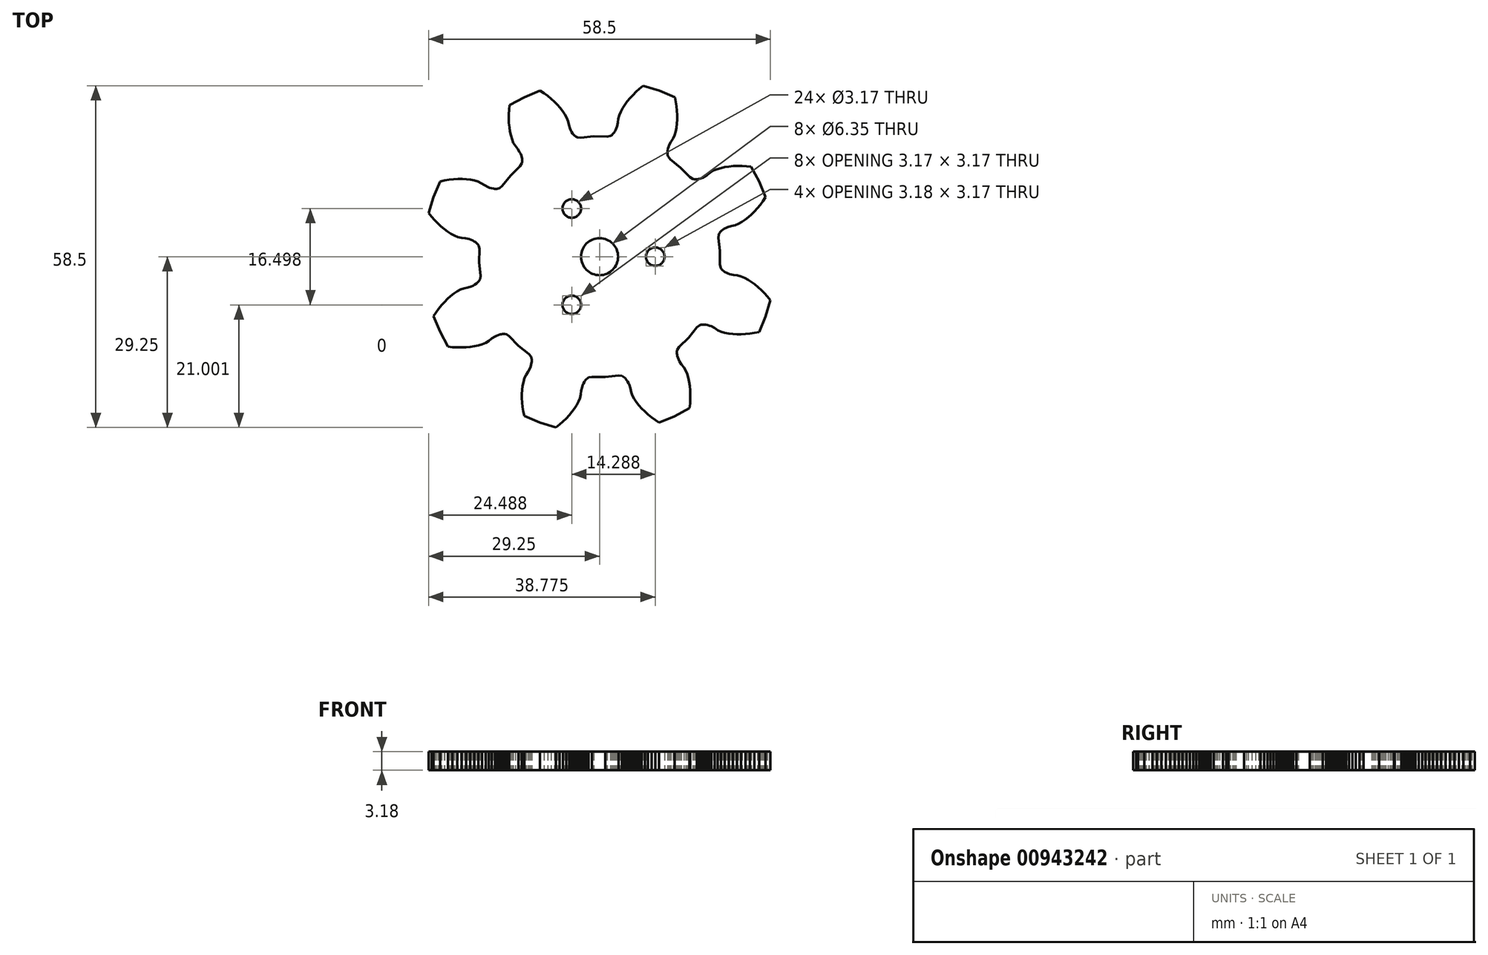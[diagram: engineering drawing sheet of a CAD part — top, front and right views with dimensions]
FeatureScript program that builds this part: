
annotation { "Feature Type Name" : "Feature", "Feature Type Description" : "" }
export const myFeature = defineFeature(function(context is Context, id is Id, definition is map)
    precondition{}
    {
        {
            var Q0;
            Q0=qCreatedBy(makeId("Top.planeOp"),FACE);
            var sketch = newSketch(context, id + "F0", { "sketchPlane" : qUnion([Q0])});
            skLineSegment(sketch, "E0", {"start": v(-20.57, 1.3) * mm, "end": v(-20.69, 1.86) * mm});
            skLineSegment(sketch, "E1", {"start": v(-20.69, 1.86) * mm, "end": v(-20.83, 2.1) * mm});
            skLineSegment(sketch, "E2", {"start": v(-20.83, 2.1) * mm, "end": v(-20.97, 2.26) * mm});
            skLineSegment(sketch, "E3", {"start": v(-20.97, 2.26) * mm, "end": v(-21.12, 2.4) * mm});
            skLineSegment(sketch, "E4", {"start": v(-21.12, 2.4) * mm, "end": v(-21.26, 2.5) * mm});
            skLineSegment(sketch, "E5", {"start": v(-21.26, 2.5) * mm, "end": v(-21.41, 2.6) * mm});
            skLineSegment(sketch, "E6", {"start": v(-21.41, 2.6) * mm, "end": v(-21.71, 2.77) * mm});
            skLineSegment(sketch, "E7", {"start": v(-21.71, 2.77) * mm, "end": v(-22.02, 2.9) * mm});
            skLineSegment(sketch, "E8", {"start": v(-22.02, 2.9) * mm, "end": v(-22.33, 3) * mm});
            skLineSegment(sketch, "E9", {"start": v(-22.33, 3) * mm, "end": v(-22.95, 3.13) * mm});
            skLineSegment(sketch, "E10", {"start": v(-22.95, 3.13) * mm, "end": v(-23.59, 3.2) * mm});
            skLineSegment(sketch, "E11", {"start": v(-23.59, 3.2) * mm, "end": v(-24.21, 3.36) * mm});
            skLineSegment(sketch, "E12", {"start": v(-24.21, 3.36) * mm, "end": v(-24.82, 3.62) * mm});
            skLineSegment(sketch, "E13", {"start": v(-24.82, 3.62) * mm, "end": v(-25.41, 3.95) * mm});
            skLineSegment(sketch, "E14", {"start": v(-25.41, 3.95) * mm, "end": v(-26, 4.32) * mm});
            skLineSegment(sketch, "E15", {"start": v(-26, 4.32) * mm, "end": v(-26.58, 4.74) * mm});
            skLineSegment(sketch, "E16", {"start": v(-26.58, 4.74) * mm, "end": v(-27.14, 5.2) * mm});
            skLineSegment(sketch, "E17", {"start": v(-27.14, 5.2) * mm, "end": v(-27.69, 5.71) * mm});
            skLineSegment(sketch, "E18", {"start": v(-27.69, 5.71) * mm, "end": v(-28.22, 6.26) * mm});
            skLineSegment(sketch, "E19", {"start": v(-28.22, 6.26) * mm, "end": v(-28.74, 6.84) * mm});
            skLineSegment(sketch, "E20", {"start": v(-28.74, 6.84) * mm, "end": v(-29.25, 7.46) * mm});
            skLineSegment(sketch, "E21", {"start": v(-29.25, 7.46) * mm, "end": v(-28.4, 10.23) * mm});
            skLineSegment(sketch, "E22", {"start": v(-28.4, 10.23) * mm, "end": v(-27.3, 12.9) * mm});
            skLineSegment(sketch, "E23", {"start": v(-27.3, 12.9) * mm, "end": v(-26.5, 13.05) * mm});
            skLineSegment(sketch, "E24", {"start": v(-26.5, 13.05) * mm, "end": v(-25.74, 13.17) * mm});
            skLineSegment(sketch, "E25", {"start": v(-25.74, 13.17) * mm, "end": v(-24.98, 13.25) * mm});
            skLineSegment(sketch, "E26", {"start": v(-24.98, 13.25) * mm, "end": v(-24.23, 13.29) * mm});
            skLineSegment(sketch, "E27", {"start": v(-24.23, 13.29) * mm, "end": v(-23.5, 13.29) * mm});
            skLineSegment(sketch, "E28", {"start": v(-23.5, 13.29) * mm, "end": v(-22.79, 13.24) * mm});
            skLineSegment(sketch, "E29", {"start": v(-22.79, 13.24) * mm, "end": v(-22.1, 13.16) * mm});
            skLineSegment(sketch, "E30", {"start": v(-22.1, 13.16) * mm, "end": v(-21.43, 13.03) * mm});
            skLineSegment(sketch, "E31", {"start": v(-21.43, 13.03) * mm, "end": v(-20.8, 12.85) * mm});
            skLineSegment(sketch, "E32", {"start": v(-20.8, 12.85) * mm, "end": v(-20.21, 12.57) * mm});
            skLineSegment(sketch, "E33", {"start": v(-20.21, 12.57) * mm, "end": v(-19.68, 12.22) * mm});
            skLineSegment(sketch, "E34", {"start": v(-19.68, 12.22) * mm, "end": v(-19.11, 11.92) * mm});
            skLineSegment(sketch, "E35", {"start": v(-19.11, 11.92) * mm, "end": v(-18.81, 11.8) * mm});
            skLineSegment(sketch, "E36", {"start": v(-18.81, 11.8) * mm, "end": v(-18.5, 11.7) * mm});
            skLineSegment(sketch, "E37", {"start": v(-18.5, 11.7) * mm, "end": v(-18.16, 11.64) * mm});
            skLineSegment(sketch, "E38", {"start": v(-18.16, 11.64) * mm, "end": v(-17.98, 11.62) * mm});
            skLineSegment(sketch, "E39", {"start": v(-17.98, 11.62) * mm, "end": v(-17.8, 11.62) * mm});
            skLineSegment(sketch, "E40", {"start": v(-17.8, 11.62) * mm, "end": v(-17.6, 11.63) * mm});
            skLineSegment(sketch, "E41", {"start": v(-17.6, 11.63) * mm, "end": v(-17.38, 11.67) * mm});
            skLineSegment(sketch, "E42", {"start": v(-17.38, 11.67) * mm, "end": v(-17.13, 11.75) * mm});
            skLineSegment(sketch, "E43", {"start": v(-17.13, 11.75) * mm, "end": v(-16.68, 12.1) * mm});
            skLineSegment(sketch, "E44", {"start": v(-16.68, 12.1) * mm, "end": v(-15.25, 13.87) * mm});
            skLineSegment(sketch, "E45", {"start": v(-15.25, 13.87) * mm, "end": v(-13.62, 15.47) * mm});
            skLineSegment(sketch, "E46", {"start": v(-13.62, 15.47) * mm, "end": v(-13.31, 15.95) * mm});
            skLineSegment(sketch, "E47", {"start": v(-13.31, 15.95) * mm, "end": v(-13.25, 16.2) * mm});
            skLineSegment(sketch, "E48", {"start": v(-13.25, 16.2) * mm, "end": v(-13.23, 16.43) * mm});
            skLineSegment(sketch, "E49", {"start": v(-13.23, 16.43) * mm, "end": v(-13.24, 16.62) * mm});
            skLineSegment(sketch, "E50", {"start": v(-13.24, 16.62) * mm, "end": v(-13.26, 16.8) * mm});
            skLineSegment(sketch, "E51", {"start": v(-13.26, 16.8) * mm, "end": v(-13.3, 16.98) * mm});
            skLineSegment(sketch, "E52", {"start": v(-13.3, 16.98) * mm, "end": v(-13.4, 17.31) * mm});
            skLineSegment(sketch, "E53", {"start": v(-13.4, 17.31) * mm, "end": v(-13.52, 17.62) * mm});
            skLineSegment(sketch, "E54", {"start": v(-13.52, 17.62) * mm, "end": v(-13.67, 17.9) * mm});
            skLineSegment(sketch, "E55", {"start": v(-13.67, 17.9) * mm, "end": v(-14.02, 18.45) * mm});
            skLineSegment(sketch, "E56", {"start": v(-14.02, 18.45) * mm, "end": v(-14.42, 18.94) * mm});
            skLineSegment(sketch, "E57", {"start": v(-14.42, 18.94) * mm, "end": v(-14.75, 19.5) * mm});
            skLineSegment(sketch, "E58", {"start": v(-14.75, 19.5) * mm, "end": v(-14.99, 20.1) * mm});
            skLineSegment(sketch, "E59", {"start": v(-14.99, 20.1) * mm, "end": v(-15.18, 20.76) * mm});
            skLineSegment(sketch, "E60", {"start": v(-15.18, 20.76) * mm, "end": v(-15.33, 21.44) * mm});
            skLineSegment(sketch, "E61", {"start": v(-15.33, 21.44) * mm, "end": v(-15.44, 22.15) * mm});
            skLineSegment(sketch, "E62", {"start": v(-15.44, 22.15) * mm, "end": v(-15.5, 22.87) * mm});
            skLineSegment(sketch, "E63", {"start": v(-15.5, 22.87) * mm, "end": v(-15.54, 23.62) * mm});
            skLineSegment(sketch, "E64", {"start": v(-15.54, 23.62) * mm, "end": v(-15.53, 24.38) * mm});
            skLineSegment(sketch, "E65", {"start": v(-15.53, 24.38) * mm, "end": v(-15.49, 25.16) * mm});
            skLineSegment(sketch, "E66", {"start": v(-15.49, 25.16) * mm, "end": v(-15.4, 25.96) * mm});
            skLineSegment(sketch, "E67", {"start": v(-15.4, 25.96) * mm, "end": v(-12.85, 27.31) * mm});
            skLineSegment(sketch, "E68", {"start": v(-12.85, 27.31) * mm, "end": v(-10.18, 28.42) * mm});
            skLineSegment(sketch, "E69", {"start": v(-10.18, 28.42) * mm, "end": v(-9.52, 27.97) * mm});
            skLineSegment(sketch, "E70", {"start": v(-9.52, 27.97) * mm, "end": v(-8.89, 27.5) * mm});
            skLineSegment(sketch, "E71", {"start": v(-8.89, 27.5) * mm, "end": v(-8.3, 27.03) * mm});
            skLineSegment(sketch, "E72", {"start": v(-8.3, 27.03) * mm, "end": v(-7.74, 26.53) * mm});
            skLineSegment(sketch, "E73", {"start": v(-7.74, 26.53) * mm, "end": v(-7.22, 26.01) * mm});
            skLineSegment(sketch, "E74", {"start": v(-7.22, 26.01) * mm, "end": v(-6.75, 25.48) * mm});
            skLineSegment(sketch, "E75", {"start": v(-6.75, 25.48) * mm, "end": v(-6.32, 24.93) * mm});
            skLineSegment(sketch, "E76", {"start": v(-6.32, 24.93) * mm, "end": v(-5.94, 24.37) * mm});
            skLineSegment(sketch, "E77", {"start": v(-5.94, 24.37) * mm, "end": v(-5.62, 23.79) * mm});
            skLineSegment(sketch, "E78", {"start": v(-5.62, 23.79) * mm, "end": v(-5.4, 23.18) * mm});
            skLineSegment(sketch, "E79", {"start": v(-5.4, 23.18) * mm, "end": v(-5.28, 22.56) * mm});
            skLineSegment(sketch, "E80", {"start": v(-5.28, 22.56) * mm, "end": v(-5.08, 21.95) * mm});
            skLineSegment(sketch, "E81", {"start": v(-5.08, 21.95) * mm, "end": v(-4.96, 21.65) * mm});
            skLineSegment(sketch, "E82", {"start": v(-4.96, 21.65) * mm, "end": v(-4.8, 21.36) * mm});
            skLineSegment(sketch, "E83", {"start": v(-4.8, 21.36) * mm, "end": v(-4.61, 21.07) * mm});
            skLineSegment(sketch, "E84", {"start": v(-4.61, 21.07) * mm, "end": v(-4.5, 20.93) * mm});
            skLineSegment(sketch, "E85", {"start": v(-4.5, 20.93) * mm, "end": v(-4.37, 20.8) * mm});
            skLineSegment(sketch, "E86", {"start": v(-4.37, 20.8) * mm, "end": v(-4.22, 20.67) * mm});
            skLineSegment(sketch, "E87", {"start": v(-4.22, 20.67) * mm, "end": v(-4.04, 20.54) * mm});
            skLineSegment(sketch, "E88", {"start": v(-4.04, 20.54) * mm, "end": v(-3.8, 20.42) * mm});
            skLineSegment(sketch, "E89", {"start": v(-3.8, 20.42) * mm, "end": v(-3.24, 20.36) * mm});
            skLineSegment(sketch, "E90", {"start": v(-3.24, 20.36) * mm, "end": v(-0.97, 20.6) * mm});
            skLineSegment(sketch, "E91", {"start": v(-0.97, 20.6) * mm, "end": v(1.3, 20.57) * mm});
            skLineSegment(sketch, "E92", {"start": v(1.3, 20.57) * mm, "end": v(1.86, 20.69) * mm});
            skLineSegment(sketch, "E93", {"start": v(1.86, 20.69) * mm, "end": v(2.1, 20.83) * mm});
            skLineSegment(sketch, "E94", {"start": v(2.1, 20.83) * mm, "end": v(2.26, 20.97) * mm});
            skLineSegment(sketch, "E95", {"start": v(2.26, 20.97) * mm, "end": v(2.4, 21.12) * mm});
            skLineSegment(sketch, "E96", {"start": v(2.4, 21.12) * mm, "end": v(2.5, 21.26) * mm});
            skLineSegment(sketch, "E97", {"start": v(2.5, 21.26) * mm, "end": v(2.6, 21.41) * mm});
            skLineSegment(sketch, "E98", {"start": v(2.6, 21.41) * mm, "end": v(2.77, 21.71) * mm});
            skLineSegment(sketch, "E99", {"start": v(2.77, 21.71) * mm, "end": v(2.9, 22.02) * mm});
            skLineSegment(sketch, "E100", {"start": v(2.9, 22.02) * mm, "end": v(3, 22.33) * mm});
            skLineSegment(sketch, "E101", {"start": v(3, 22.33) * mm, "end": v(3.13, 22.95) * mm});
            skLineSegment(sketch, "E102", {"start": v(3.13, 22.95) * mm, "end": v(3.2, 23.59) * mm});
            skLineSegment(sketch, "E103", {"start": v(3.2, 23.59) * mm, "end": v(3.36, 24.21) * mm});
            skLineSegment(sketch, "E104", {"start": v(3.36, 24.21) * mm, "end": v(3.62, 24.82) * mm});
            skLineSegment(sketch, "E105", {"start": v(3.62, 24.82) * mm, "end": v(3.95, 25.41) * mm});
            skLineSegment(sketch, "E106", {"start": v(3.95, 25.41) * mm, "end": v(4.32, 26) * mm});
            skLineSegment(sketch, "E107", {"start": v(4.32, 26) * mm, "end": v(4.74, 26.58) * mm});
            skLineSegment(sketch, "E108", {"start": v(4.74, 26.58) * mm, "end": v(5.2, 27.14) * mm});
            skLineSegment(sketch, "E109", {"start": v(5.2, 27.14) * mm, "end": v(5.71, 27.69) * mm});
            skLineSegment(sketch, "E110", {"start": v(5.71, 27.69) * mm, "end": v(6.26, 28.22) * mm});
            skLineSegment(sketch, "E111", {"start": v(6.26, 28.22) * mm, "end": v(6.84, 28.74) * mm});
            skLineSegment(sketch, "E112", {"start": v(6.84, 28.74) * mm, "end": v(7.46, 29.25) * mm});
            skLineSegment(sketch, "E113", {"start": v(7.46, 29.25) * mm, "end": v(10.23, 28.4) * mm});
            skLineSegment(sketch, "E114", {"start": v(10.23, 28.4) * mm, "end": v(12.9, 27.3) * mm});
            skLineSegment(sketch, "E115", {"start": v(12.9, 27.3) * mm, "end": v(13.05, 26.5) * mm});
            skLineSegment(sketch, "E116", {"start": v(13.05, 26.5) * mm, "end": v(13.17, 25.74) * mm});
            skLineSegment(sketch, "E117", {"start": v(13.17, 25.74) * mm, "end": v(13.25, 24.98) * mm});
            skLineSegment(sketch, "E118", {"start": v(13.25, 24.98) * mm, "end": v(13.29, 24.23) * mm});
            skLineSegment(sketch, "E119", {"start": v(13.29, 24.23) * mm, "end": v(13.29, 23.5) * mm});
            skLineSegment(sketch, "E120", {"start": v(13.29, 23.5) * mm, "end": v(13.24, 22.79) * mm});
            skLineSegment(sketch, "E121", {"start": v(13.24, 22.79) * mm, "end": v(13.16, 22.1) * mm});
            skLineSegment(sketch, "E122", {"start": v(13.16, 22.1) * mm, "end": v(13.03, 21.43) * mm});
            skLineSegment(sketch, "E123", {"start": v(13.03, 21.43) * mm, "end": v(12.85, 20.8) * mm});
            skLineSegment(sketch, "E124", {"start": v(12.85, 20.8) * mm, "end": v(12.57, 20.21) * mm});
            skLineSegment(sketch, "E125", {"start": v(12.57, 20.21) * mm, "end": v(12.22, 19.68) * mm});
            skLineSegment(sketch, "E126", {"start": v(12.22, 19.68) * mm, "end": v(11.92, 19.11) * mm});
            skLineSegment(sketch, "E127", {"start": v(11.92, 19.11) * mm, "end": v(11.8, 18.81) * mm});
            skLineSegment(sketch, "E128", {"start": v(11.8, 18.81) * mm, "end": v(11.7, 18.5) * mm});
            skLineSegment(sketch, "E129", {"start": v(11.7, 18.5) * mm, "end": v(11.64, 18.16) * mm});
            skLineSegment(sketch, "E130", {"start": v(11.64, 18.16) * mm, "end": v(11.62, 17.98) * mm});
            skLineSegment(sketch, "E131", {"start": v(11.62, 17.98) * mm, "end": v(11.62, 17.8) * mm});
            skLineSegment(sketch, "E132", {"start": v(11.62, 17.8) * mm, "end": v(11.63, 17.6) * mm});
            skLineSegment(sketch, "E133", {"start": v(11.63, 17.6) * mm, "end": v(11.67, 17.38) * mm});
            skLineSegment(sketch, "E134", {"start": v(11.67, 17.38) * mm, "end": v(11.75, 17.13) * mm});
            skLineSegment(sketch, "E135", {"start": v(11.75, 17.13) * mm, "end": v(12.1, 16.68) * mm});
            skLineSegment(sketch, "E136", {"start": v(12.1, 16.68) * mm, "end": v(13.87, 15.25) * mm});
            skLineSegment(sketch, "E137", {"start": v(13.87, 15.25) * mm, "end": v(15.47, 13.62) * mm});
            skLineSegment(sketch, "E138", {"start": v(15.47, 13.62) * mm, "end": v(15.95, 13.31) * mm});
            skLineSegment(sketch, "E139", {"start": v(15.95, 13.31) * mm, "end": v(16.2, 13.25) * mm});
            skLineSegment(sketch, "E140", {"start": v(16.2, 13.25) * mm, "end": v(16.43, 13.23) * mm});
            skLineSegment(sketch, "E141", {"start": v(16.43, 13.23) * mm, "end": v(16.62, 13.24) * mm});
            skLineSegment(sketch, "E142", {"start": v(16.62, 13.24) * mm, "end": v(16.8, 13.26) * mm});
            skLineSegment(sketch, "E143", {"start": v(16.8, 13.26) * mm, "end": v(16.98, 13.3) * mm});
            skLineSegment(sketch, "E144", {"start": v(16.98, 13.3) * mm, "end": v(17.31, 13.4) * mm});
            skLineSegment(sketch, "E145", {"start": v(17.31, 13.4) * mm, "end": v(17.62, 13.52) * mm});
            skLineSegment(sketch, "E146", {"start": v(17.62, 13.52) * mm, "end": v(17.9, 13.67) * mm});
            skLineSegment(sketch, "E147", {"start": v(17.9, 13.67) * mm, "end": v(18.45, 14.02) * mm});
            skLineSegment(sketch, "E148", {"start": v(18.45, 14.02) * mm, "end": v(18.94, 14.42) * mm});
            skLineSegment(sketch, "E149", {"start": v(18.94, 14.42) * mm, "end": v(19.5, 14.75) * mm});
            skLineSegment(sketch, "E150", {"start": v(19.5, 14.75) * mm, "end": v(20.1, 14.99) * mm});
            skLineSegment(sketch, "E151", {"start": v(20.1, 14.99) * mm, "end": v(20.76, 15.18) * mm});
            skLineSegment(sketch, "E152", {"start": v(20.76, 15.18) * mm, "end": v(21.44, 15.33) * mm});
            skLineSegment(sketch, "E153", {"start": v(21.44, 15.33) * mm, "end": v(22.15, 15.44) * mm});
            skLineSegment(sketch, "E154", {"start": v(22.15, 15.44) * mm, "end": v(22.87, 15.5) * mm});
            skLineSegment(sketch, "E155", {"start": v(22.87, 15.5) * mm, "end": v(23.62, 15.54) * mm});
            skLineSegment(sketch, "E156", {"start": v(23.62, 15.54) * mm, "end": v(24.38, 15.53) * mm});
            skLineSegment(sketch, "E157", {"start": v(24.38, 15.53) * mm, "end": v(25.16, 15.49) * mm});
            skLineSegment(sketch, "E158", {"start": v(25.16, 15.49) * mm, "end": v(25.96, 15.4) * mm});
            skLineSegment(sketch, "E159", {"start": v(25.96, 15.4) * mm, "end": v(27.31, 12.85) * mm});
            skLineSegment(sketch, "E160", {"start": v(27.31, 12.85) * mm, "end": v(28.42, 10.18) * mm});
            skLineSegment(sketch, "E161", {"start": v(28.42, 10.18) * mm, "end": v(27.97, 9.52) * mm});
            skLineSegment(sketch, "E162", {"start": v(27.97, 9.52) * mm, "end": v(27.5, 8.89) * mm});
            skLineSegment(sketch, "E163", {"start": v(27.5, 8.89) * mm, "end": v(27.03, 8.3) * mm});
            skLineSegment(sketch, "E164", {"start": v(27.03, 8.3) * mm, "end": v(26.53, 7.74) * mm});
            skLineSegment(sketch, "E165", {"start": v(26.53, 7.74) * mm, "end": v(26.01, 7.22) * mm});
            skLineSegment(sketch, "E166", {"start": v(26.01, 7.22) * mm, "end": v(25.48, 6.75) * mm});
            skLineSegment(sketch, "E167", {"start": v(25.48, 6.75) * mm, "end": v(24.93, 6.32) * mm});
            skLineSegment(sketch, "E168", {"start": v(24.93, 6.32) * mm, "end": v(24.37, 5.94) * mm});
            skLineSegment(sketch, "E169", {"start": v(24.37, 5.94) * mm, "end": v(23.79, 5.62) * mm});
            skLineSegment(sketch, "E170", {"start": v(23.79, 5.62) * mm, "end": v(23.18, 5.4) * mm});
            skLineSegment(sketch, "E171", {"start": v(23.18, 5.4) * mm, "end": v(22.56, 5.28) * mm});
            skLineSegment(sketch, "E172", {"start": v(22.56, 5.28) * mm, "end": v(21.95, 5.09) * mm});
            skLineSegment(sketch, "E173", {"start": v(21.95, 5.09) * mm, "end": v(21.65, 4.96) * mm});
            skLineSegment(sketch, "E174", {"start": v(21.65, 4.96) * mm, "end": v(21.36, 4.8) * mm});
            skLineSegment(sketch, "E175", {"start": v(21.36, 4.8) * mm, "end": v(21.07, 4.61) * mm});
            skLineSegment(sketch, "E176", {"start": v(21.07, 4.61) * mm, "end": v(20.93, 4.5) * mm});
            skLineSegment(sketch, "E177", {"start": v(20.93, 4.5) * mm, "end": v(20.8, 4.37) * mm});
            skLineSegment(sketch, "E178", {"start": v(20.8, 4.37) * mm, "end": v(20.67, 4.22) * mm});
            skLineSegment(sketch, "E179", {"start": v(20.67, 4.22) * mm, "end": v(20.54, 4.04) * mm});
            skLineSegment(sketch, "E180", {"start": v(20.54, 4.04) * mm, "end": v(20.42, 3.8) * mm});
            skLineSegment(sketch, "E181", {"start": v(20.42, 3.8) * mm, "end": v(20.36, 3.24) * mm});
            skLineSegment(sketch, "E182", {"start": v(20.36, 3.24) * mm, "end": v(20.6, 0.97) * mm});
            skLineSegment(sketch, "E183", {"start": v(20.6, 0.97) * mm, "end": v(20.57, -1.3) * mm});
            skLineSegment(sketch, "E184", {"start": v(20.57, -1.3) * mm, "end": v(20.69, -1.86) * mm});
            skLineSegment(sketch, "E185", {"start": v(20.69, -1.86) * mm, "end": v(20.83, -2.09) * mm});
            skLineSegment(sketch, "E186", {"start": v(20.83, -2.09) * mm, "end": v(20.97, -2.26) * mm});
            skLineSegment(sketch, "E187", {"start": v(20.97, -2.26) * mm, "end": v(21.12, -2.4) * mm});
            skLineSegment(sketch, "E188", {"start": v(21.12, -2.4) * mm, "end": v(21.26, -2.5) * mm});
            skLineSegment(sketch, "E189", {"start": v(21.26, -2.5) * mm, "end": v(21.41, -2.6) * mm});
            skLineSegment(sketch, "E190", {"start": v(21.41, -2.6) * mm, "end": v(21.71, -2.77) * mm});
            skLineSegment(sketch, "E191", {"start": v(21.71, -2.77) * mm, "end": v(22.02, -2.9) * mm});
            skLineSegment(sketch, "E192", {"start": v(22.02, -2.9) * mm, "end": v(22.33, -3) * mm});
            skLineSegment(sketch, "E193", {"start": v(22.33, -3) * mm, "end": v(22.95, -3.13) * mm});
            skLineSegment(sketch, "E194", {"start": v(22.95, -3.13) * mm, "end": v(23.59, -3.2) * mm});
            skLineSegment(sketch, "E195", {"start": v(23.59, -3.2) * mm, "end": v(24.21, -3.36) * mm});
            skLineSegment(sketch, "E196", {"start": v(24.21, -3.36) * mm, "end": v(24.82, -3.62) * mm});
            skLineSegment(sketch, "E197", {"start": v(24.82, -3.62) * mm, "end": v(25.41, -3.95) * mm});
            skLineSegment(sketch, "E198", {"start": v(25.41, -3.95) * mm, "end": v(26, -4.32) * mm});
            skLineSegment(sketch, "E199", {"start": v(26, -4.32) * mm, "end": v(26.58, -4.74) * mm});
            skLineSegment(sketch, "E200", {"start": v(26.58, -4.74) * mm, "end": v(27.14, -5.2) * mm});
            skLineSegment(sketch, "E201", {"start": v(27.14, -5.2) * mm, "end": v(27.69, -5.71) * mm});
            skLineSegment(sketch, "E202", {"start": v(27.69, -5.71) * mm, "end": v(28.22, -6.26) * mm});
            skLineSegment(sketch, "E203", {"start": v(28.22, -6.26) * mm, "end": v(28.74, -6.84) * mm});
            skLineSegment(sketch, "E204", {"start": v(28.74, -6.84) * mm, "end": v(29.25, -7.46) * mm});
            skLineSegment(sketch, "E205", {"start": v(29.25, -7.46) * mm, "end": v(28.4, -10.22) * mm});
            skLineSegment(sketch, "E206", {"start": v(28.4, -10.22) * mm, "end": v(27.3, -12.9) * mm});
            skLineSegment(sketch, "E207", {"start": v(27.3, -12.9) * mm, "end": v(26.5, -13.05) * mm});
            skLineSegment(sketch, "E208", {"start": v(26.5, -13.05) * mm, "end": v(25.74, -13.17) * mm});
            skLineSegment(sketch, "E209", {"start": v(25.74, -13.17) * mm, "end": v(24.98, -13.25) * mm});
            skLineSegment(sketch, "E210", {"start": v(24.98, -13.25) * mm, "end": v(24.23, -13.29) * mm});
            skLineSegment(sketch, "E211", {"start": v(24.23, -13.29) * mm, "end": v(23.5, -13.29) * mm});
            skLineSegment(sketch, "E212", {"start": v(23.5, -13.29) * mm, "end": v(22.79, -13.24) * mm});
            skLineSegment(sketch, "E213", {"start": v(22.79, -13.24) * mm, "end": v(22.1, -13.16) * mm});
            skLineSegment(sketch, "E214", {"start": v(22.1, -13.16) * mm, "end": v(21.43, -13.03) * mm});
            skLineSegment(sketch, "E215", {"start": v(21.43, -13.03) * mm, "end": v(20.8, -12.85) * mm});
            skLineSegment(sketch, "E216", {"start": v(20.8, -12.85) * mm, "end": v(20.21, -12.57) * mm});
            skLineSegment(sketch, "E217", {"start": v(20.21, -12.57) * mm, "end": v(19.68, -12.22) * mm});
            skLineSegment(sketch, "E218", {"start": v(19.68, -12.22) * mm, "end": v(19.11, -11.92) * mm});
            skLineSegment(sketch, "E219", {"start": v(19.11, -11.92) * mm, "end": v(18.81, -11.8) * mm});
            skLineSegment(sketch, "E220", {"start": v(18.81, -11.8) * mm, "end": v(18.5, -11.7) * mm});
            skLineSegment(sketch, "E221", {"start": v(18.5, -11.7) * mm, "end": v(18.16, -11.64) * mm});
            skLineSegment(sketch, "E222", {"start": v(18.16, -11.64) * mm, "end": v(17.98, -11.62) * mm});
            skLineSegment(sketch, "E223", {"start": v(17.98, -11.62) * mm, "end": v(17.8, -11.62) * mm});
            skLineSegment(sketch, "E224", {"start": v(17.8, -11.62) * mm, "end": v(17.6, -11.63) * mm});
            skLineSegment(sketch, "E225", {"start": v(17.6, -11.63) * mm, "end": v(17.38, -11.67) * mm});
            skLineSegment(sketch, "E226", {"start": v(17.38, -11.67) * mm, "end": v(17.13, -11.75) * mm});
            skLineSegment(sketch, "E227", {"start": v(17.13, -11.75) * mm, "end": v(16.68, -12.1) * mm});
            skLineSegment(sketch, "E228", {"start": v(16.68, -12.1) * mm, "end": v(15.25, -13.87) * mm});
            skLineSegment(sketch, "E229", {"start": v(15.25, -13.87) * mm, "end": v(13.62, -15.47) * mm});
            skLineSegment(sketch, "E230", {"start": v(13.62, -15.47) * mm, "end": v(13.31, -15.95) * mm});
            skLineSegment(sketch, "E231", {"start": v(13.31, -15.95) * mm, "end": v(13.25, -16.2) * mm});
            skLineSegment(sketch, "E232", {"start": v(13.25, -16.2) * mm, "end": v(13.23, -16.43) * mm});
            skLineSegment(sketch, "E233", {"start": v(13.23, -16.43) * mm, "end": v(13.24, -16.62) * mm});
            skLineSegment(sketch, "E234", {"start": v(13.24, -16.62) * mm, "end": v(13.26, -16.8) * mm});
            skLineSegment(sketch, "E235", {"start": v(13.26, -16.8) * mm, "end": v(13.3, -16.98) * mm});
            skLineSegment(sketch, "E236", {"start": v(13.3, -16.98) * mm, "end": v(13.4, -17.31) * mm});
            skLineSegment(sketch, "E237", {"start": v(13.4, -17.31) * mm, "end": v(13.52, -17.62) * mm});
            skLineSegment(sketch, "E238", {"start": v(13.52, -17.62) * mm, "end": v(13.67, -17.9) * mm});
            skLineSegment(sketch, "E239", {"start": v(13.67, -17.9) * mm, "end": v(14.02, -18.45) * mm});
            skLineSegment(sketch, "E240", {"start": v(14.02, -18.45) * mm, "end": v(14.42, -18.94) * mm});
            skLineSegment(sketch, "E241", {"start": v(14.42, -18.94) * mm, "end": v(14.75, -19.5) * mm});
            skLineSegment(sketch, "E242", {"start": v(14.75, -19.5) * mm, "end": v(14.99, -20.1) * mm});
            skLineSegment(sketch, "E243", {"start": v(14.99, -20.1) * mm, "end": v(15.18, -20.76) * mm});
            skLineSegment(sketch, "E244", {"start": v(15.18, -20.76) * mm, "end": v(15.33, -21.44) * mm});
            skLineSegment(sketch, "E245", {"start": v(15.33, -21.44) * mm, "end": v(15.44, -22.15) * mm});
            skLineSegment(sketch, "E246", {"start": v(15.44, -22.15) * mm, "end": v(15.5, -22.87) * mm});
            skLineSegment(sketch, "E247", {"start": v(15.5, -22.87) * mm, "end": v(15.54, -23.62) * mm});
            skLineSegment(sketch, "E248", {"start": v(15.54, -23.62) * mm, "end": v(15.53, -24.38) * mm});
            skLineSegment(sketch, "E249", {"start": v(15.53, -24.38) * mm, "end": v(15.49, -25.16) * mm});
            skLineSegment(sketch, "E250", {"start": v(15.49, -25.16) * mm, "end": v(15.4, -25.96) * mm});
            skLineSegment(sketch, "E251", {"start": v(15.4, -25.96) * mm, "end": v(12.85, -27.31) * mm});
            skLineSegment(sketch, "E252", {"start": v(12.85, -27.31) * mm, "end": v(10.18, -28.42) * mm});
            skLineSegment(sketch, "E253", {"start": v(10.18, -28.42) * mm, "end": v(9.52, -27.97) * mm});
            skLineSegment(sketch, "E254", {"start": v(9.52, -27.97) * mm, "end": v(8.89, -27.5) * mm});
            skLineSegment(sketch, "E255", {"start": v(8.89, -27.5) * mm, "end": v(8.3, -27.03) * mm});
            skLineSegment(sketch, "E256", {"start": v(8.3, -27.03) * mm, "end": v(7.74, -26.53) * mm});
            skLineSegment(sketch, "E257", {"start": v(7.74, -26.53) * mm, "end": v(7.22, -26.01) * mm});
            skLineSegment(sketch, "E258", {"start": v(7.22, -26.01) * mm, "end": v(6.75, -25.48) * mm});
            skLineSegment(sketch, "E259", {"start": v(6.75, -25.48) * mm, "end": v(6.32, -24.93) * mm});
            skLineSegment(sketch, "E260", {"start": v(6.32, -24.93) * mm, "end": v(5.94, -24.37) * mm});
            skLineSegment(sketch, "E261", {"start": v(5.94, -24.37) * mm, "end": v(5.62, -23.79) * mm});
            skLineSegment(sketch, "E262", {"start": v(5.62, -23.79) * mm, "end": v(5.4, -23.18) * mm});
            skLineSegment(sketch, "E263", {"start": v(5.4, -23.18) * mm, "end": v(5.28, -22.56) * mm});
            skLineSegment(sketch, "E264", {"start": v(5.28, -22.56) * mm, "end": v(5.09, -21.95) * mm});
            skLineSegment(sketch, "E265", {"start": v(5.09, -21.95) * mm, "end": v(4.96, -21.65) * mm});
            skLineSegment(sketch, "E266", {"start": v(4.96, -21.65) * mm, "end": v(4.8, -21.36) * mm});
            skLineSegment(sketch, "E267", {"start": v(4.8, -21.36) * mm, "end": v(4.61, -21.07) * mm});
            skLineSegment(sketch, "E268", {"start": v(4.61, -21.07) * mm, "end": v(4.5, -20.93) * mm});
            skLineSegment(sketch, "E269", {"start": v(4.5, -20.93) * mm, "end": v(4.37, -20.8) * mm});
            skLineSegment(sketch, "E270", {"start": v(4.37, -20.8) * mm, "end": v(4.22, -20.67) * mm});
            skLineSegment(sketch, "E271", {"start": v(4.22, -20.67) * mm, "end": v(4.04, -20.54) * mm});
            skLineSegment(sketch, "E272", {"start": v(4.04, -20.54) * mm, "end": v(3.8, -20.42) * mm});
            skLineSegment(sketch, "E273", {"start": v(3.8, -20.42) * mm, "end": v(3.24, -20.36) * mm});
            skLineSegment(sketch, "E274", {"start": v(3.24, -20.36) * mm, "end": v(0.97, -20.6) * mm});
            skLineSegment(sketch, "E275", {"start": v(0.97, -20.6) * mm, "end": v(-1.3, -20.57) * mm});
            skLineSegment(sketch, "E276", {"start": v(-1.3, -20.57) * mm, "end": v(-1.86, -20.69) * mm});
            skLineSegment(sketch, "E277", {"start": v(-1.86, -20.69) * mm, "end": v(-2.09, -20.83) * mm});
            skLineSegment(sketch, "E278", {"start": v(-2.09, -20.83) * mm, "end": v(-2.26, -20.97) * mm});
            skLineSegment(sketch, "E279", {"start": v(-2.26, -20.97) * mm, "end": v(-2.4, -21.12) * mm});
            skLineSegment(sketch, "E280", {"start": v(-2.4, -21.12) * mm, "end": v(-2.5, -21.26) * mm});
            skLineSegment(sketch, "E281", {"start": v(-2.5, -21.26) * mm, "end": v(-2.6, -21.41) * mm});
            skLineSegment(sketch, "E282", {"start": v(-2.6, -21.41) * mm, "end": v(-2.77, -21.71) * mm});
            skLineSegment(sketch, "E283", {"start": v(-2.77, -21.71) * mm, "end": v(-2.9, -22.02) * mm});
            skLineSegment(sketch, "E284", {"start": v(-2.9, -22.02) * mm, "end": v(-3, -22.33) * mm});
            skLineSegment(sketch, "E285", {"start": v(-3, -22.33) * mm, "end": v(-3.13, -22.95) * mm});
            skLineSegment(sketch, "E286", {"start": v(-3.13, -22.95) * mm, "end": v(-3.2, -23.59) * mm});
            skLineSegment(sketch, "E287", {"start": v(-3.2, -23.59) * mm, "end": v(-3.36, -24.21) * mm});
            skLineSegment(sketch, "E288", {"start": v(-3.36, -24.21) * mm, "end": v(-3.62, -24.82) * mm});
            skLineSegment(sketch, "E289", {"start": v(-3.62, -24.82) * mm, "end": v(-3.95, -25.41) * mm});
            skLineSegment(sketch, "E290", {"start": v(-3.95, -25.41) * mm, "end": v(-4.32, -26) * mm});
            skLineSegment(sketch, "E291", {"start": v(-4.32, -26) * mm, "end": v(-4.74, -26.58) * mm});
            skLineSegment(sketch, "E292", {"start": v(-4.74, -26.58) * mm, "end": v(-5.2, -27.14) * mm});
            skLineSegment(sketch, "E293", {"start": v(-5.2, -27.14) * mm, "end": v(-5.71, -27.69) * mm});
            skLineSegment(sketch, "E294", {"start": v(-5.71, -27.69) * mm, "end": v(-6.26, -28.22) * mm});
            skLineSegment(sketch, "E295", {"start": v(-6.26, -28.22) * mm, "end": v(-6.84, -28.74) * mm});
            skLineSegment(sketch, "E296", {"start": v(-6.84, -28.74) * mm, "end": v(-7.46, -29.25) * mm});
            skLineSegment(sketch, "E297", {"start": v(-7.46, -29.25) * mm, "end": v(-10.22, -28.4) * mm});
            skLineSegment(sketch, "E298", {"start": v(-10.22, -28.4) * mm, "end": v(-12.9, -27.3) * mm});
            skLineSegment(sketch, "E299", {"start": v(-12.9, -27.3) * mm, "end": v(-13.05, -26.5) * mm});
            skLineSegment(sketch, "E300", {"start": v(-13.05, -26.5) * mm, "end": v(-13.17, -25.74) * mm});
            skLineSegment(sketch, "E301", {"start": v(-13.17, -25.74) * mm, "end": v(-13.25, -24.98) * mm});
            skLineSegment(sketch, "E302", {"start": v(-13.25, -24.98) * mm, "end": v(-13.29, -24.23) * mm});
            skLineSegment(sketch, "E303", {"start": v(-13.29, -24.23) * mm, "end": v(-13.29, -23.5) * mm});
            skLineSegment(sketch, "E304", {"start": v(-13.29, -23.5) * mm, "end": v(-13.24, -22.79) * mm});
            skLineSegment(sketch, "E305", {"start": v(-13.24, -22.79) * mm, "end": v(-13.16, -22.1) * mm});
            skLineSegment(sketch, "E306", {"start": v(-13.16, -22.1) * mm, "end": v(-13.03, -21.43) * mm});
            skLineSegment(sketch, "E307", {"start": v(-13.03, -21.43) * mm, "end": v(-12.85, -20.8) * mm});
            skLineSegment(sketch, "E308", {"start": v(-12.85, -20.8) * mm, "end": v(-12.57, -20.21) * mm});
            skLineSegment(sketch, "E309", {"start": v(-12.57, -20.21) * mm, "end": v(-12.22, -19.68) * mm});
            skLineSegment(sketch, "E310", {"start": v(-12.22, -19.68) * mm, "end": v(-11.92, -19.11) * mm});
            skLineSegment(sketch, "E311", {"start": v(-11.92, -19.11) * mm, "end": v(-11.8, -18.81) * mm});
            skLineSegment(sketch, "E312", {"start": v(-11.8, -18.81) * mm, "end": v(-11.7, -18.5) * mm});
            skLineSegment(sketch, "E313", {"start": v(-11.7, -18.5) * mm, "end": v(-11.64, -18.16) * mm});
            skLineSegment(sketch, "E314", {"start": v(-11.64, -18.16) * mm, "end": v(-11.62, -17.98) * mm});
            skLineSegment(sketch, "E315", {"start": v(-11.62, -17.98) * mm, "end": v(-11.62, -17.8) * mm});
            skLineSegment(sketch, "E316", {"start": v(-11.62, -17.8) * mm, "end": v(-11.63, -17.6) * mm});
            skLineSegment(sketch, "E317", {"start": v(-11.63, -17.6) * mm, "end": v(-11.67, -17.38) * mm});
            skLineSegment(sketch, "E318", {"start": v(-11.67, -17.38) * mm, "end": v(-11.75, -17.13) * mm});
            skLineSegment(sketch, "E319", {"start": v(-11.75, -17.13) * mm, "end": v(-12.1, -16.68) * mm});
            skLineSegment(sketch, "E320", {"start": v(-12.1, -16.68) * mm, "end": v(-13.87, -15.25) * mm});
            skLineSegment(sketch, "E321", {"start": v(-13.87, -15.25) * mm, "end": v(-15.47, -13.62) * mm});
            skLineSegment(sketch, "E322", {"start": v(-15.47, -13.62) * mm, "end": v(-15.95, -13.31) * mm});
            skLineSegment(sketch, "E323", {"start": v(-15.95, -13.31) * mm, "end": v(-16.2, -13.25) * mm});
            skLineSegment(sketch, "E324", {"start": v(-16.2, -13.25) * mm, "end": v(-16.43, -13.23) * mm});
            skLineSegment(sketch, "E325", {"start": v(-16.43, -13.23) * mm, "end": v(-16.62, -13.24) * mm});
            skLineSegment(sketch, "E326", {"start": v(-16.62, -13.24) * mm, "end": v(-16.8, -13.26) * mm});
            skLineSegment(sketch, "E327", {"start": v(-16.8, -13.26) * mm, "end": v(-16.98, -13.3) * mm});
            skLineSegment(sketch, "E328", {"start": v(-16.98, -13.3) * mm, "end": v(-17.31, -13.4) * mm});
            skLineSegment(sketch, "E329", {"start": v(-17.31, -13.4) * mm, "end": v(-17.62, -13.52) * mm});
            skLineSegment(sketch, "E330", {"start": v(-17.62, -13.52) * mm, "end": v(-17.9, -13.67) * mm});
            skLineSegment(sketch, "E331", {"start": v(-17.9, -13.67) * mm, "end": v(-18.45, -14.02) * mm});
            skLineSegment(sketch, "E332", {"start": v(-18.45, -14.02) * mm, "end": v(-18.94, -14.42) * mm});
            skLineSegment(sketch, "E333", {"start": v(-18.94, -14.42) * mm, "end": v(-19.5, -14.75) * mm});
            skLineSegment(sketch, "E334", {"start": v(-19.5, -14.75) * mm, "end": v(-20.1, -14.99) * mm});
            skLineSegment(sketch, "E335", {"start": v(-20.1, -14.99) * mm, "end": v(-20.76, -15.18) * mm});
            skLineSegment(sketch, "E336", {"start": v(-20.76, -15.18) * mm, "end": v(-21.44, -15.33) * mm});
            skLineSegment(sketch, "E337", {"start": v(-21.44, -15.33) * mm, "end": v(-22.15, -15.44) * mm});
            skLineSegment(sketch, "E338", {"start": v(-22.15, -15.44) * mm, "end": v(-22.87, -15.5) * mm});
            skLineSegment(sketch, "E339", {"start": v(-22.87, -15.5) * mm, "end": v(-23.62, -15.54) * mm});
            skLineSegment(sketch, "E340", {"start": v(-23.62, -15.54) * mm, "end": v(-24.38, -15.53) * mm});
            skLineSegment(sketch, "E341", {"start": v(-24.38, -15.53) * mm, "end": v(-25.16, -15.49) * mm});
            skLineSegment(sketch, "E342", {"start": v(-25.16, -15.49) * mm, "end": v(-25.96, -15.4) * mm});
            skLineSegment(sketch, "E343", {"start": v(-25.96, -15.4) * mm, "end": v(-27.31, -12.85) * mm});
            skLineSegment(sketch, "E344", {"start": v(-27.31, -12.85) * mm, "end": v(-28.42, -10.18) * mm});
            skLineSegment(sketch, "E345", {"start": v(-28.42, -10.18) * mm, "end": v(-27.97, -9.52) * mm});
            skLineSegment(sketch, "E346", {"start": v(-27.97, -9.52) * mm, "end": v(-27.5, -8.89) * mm});
            skLineSegment(sketch, "E347", {"start": v(-27.5, -8.89) * mm, "end": v(-27.03, -8.3) * mm});
            skLineSegment(sketch, "E348", {"start": v(-27.03, -8.3) * mm, "end": v(-26.53, -7.74) * mm});
            skLineSegment(sketch, "E349", {"start": v(-26.53, -7.74) * mm, "end": v(-26.01, -7.22) * mm});
            skLineSegment(sketch, "E350", {"start": v(-26.01, -7.22) * mm, "end": v(-25.48, -6.75) * mm});
            skLineSegment(sketch, "E351", {"start": v(-25.48, -6.75) * mm, "end": v(-24.93, -6.32) * mm});
            skLineSegment(sketch, "E352", {"start": v(-24.93, -6.32) * mm, "end": v(-24.37, -5.94) * mm});
            skLineSegment(sketch, "E353", {"start": v(-24.37, -5.94) * mm, "end": v(-23.79, -5.62) * mm});
            skLineSegment(sketch, "E354", {"start": v(-23.79, -5.62) * mm, "end": v(-23.18, -5.4) * mm});
            skLineSegment(sketch, "E355", {"start": v(-23.18, -5.4) * mm, "end": v(-22.56, -5.28) * mm});
            skLineSegment(sketch, "E356", {"start": v(-22.56, -5.28) * mm, "end": v(-21.95, -5.08) * mm});
            skLineSegment(sketch, "E357", {"start": v(-21.95, -5.08) * mm, "end": v(-21.65, -4.96) * mm});
            skLineSegment(sketch, "E358", {"start": v(-21.65, -4.96) * mm, "end": v(-21.36, -4.8) * mm});
            skLineSegment(sketch, "E359", {"start": v(-21.36, -4.8) * mm, "end": v(-21.07, -4.61) * mm});
            skLineSegment(sketch, "E360", {"start": v(-21.07, -4.61) * mm, "end": v(-20.93, -4.5) * mm});
            skLineSegment(sketch, "E361", {"start": v(-20.93, -4.5) * mm, "end": v(-20.8, -4.37) * mm});
            skLineSegment(sketch, "E362", {"start": v(-20.8, -4.37) * mm, "end": v(-20.67, -4.22) * mm});
            skLineSegment(sketch, "E363", {"start": v(-20.67, -4.22) * mm, "end": v(-20.54, -4.04) * mm});
            skLineSegment(sketch, "E364", {"start": v(-20.54, -4.04) * mm, "end": v(-20.42, -3.8) * mm});
            skLineSegment(sketch, "E365", {"start": v(-20.42, -3.8) * mm, "end": v(-20.36, -3.24) * mm});
            skLineSegment(sketch, "E366", {"start": v(-20.36, -3.24) * mm, "end": v(-20.6, -0.97) * mm});
            skLineSegment(sketch, "E367", {"start": v(-20.6, -0.97) * mm, "end": v(-20.57, 1.3) * mm});
            skCircle(sketch, "E368", {"center": v(0, 0) * mm, "radius": 3.18 * mm});
            skSolve(sketch);
        }
        {
            var Q0;
            Q0=makeQuery(id+"F0.imprint","IMPRINT",FACE,{"disambiguationData":[TD([[makeQuery(id+"F0.imprint","IMPRINT",EDGE,{"derivedFrom":sQuery(id+"F0.wireOp",EDGE,"E0")}),-1.0]])]});
            extrude(context, id + "F1", {"entities" : qUnion([Q0]), "depth" : 3.17 * mm, "offsetDistance" : 25.4 * mm});
        }
        {
            var Q0;
            Q0=makeQuery(id+"F1.opExtrude","CAP_FACE",FACE,{"disambiguationData":[OSD([sQuery(id+"F0.wireOp",EDGE,"E0"),sQuery(id+"F0.wireOp",EDGE,"E1"),sQuery(id+"F0.wireOp",EDGE,"E2"),sQuery(id+"F0.wireOp",EDGE,"E3"),sQuery(id+"F0.wireOp",EDGE,"E4"),sQuery(id+"F0.wireOp",EDGE,"E5"),sQuery(id+"F0.wireOp",EDGE,"E6"),sQuery(id+"F0.wireOp",EDGE,"E7"),sQuery(id+"F0.wireOp",EDGE,"E8"),sQuery(id+"F0.wireOp",EDGE,"E9"),sQuery(id+"F0.wireOp",EDGE,"E10"),sQuery(id+"F0.wireOp",EDGE,"E11"),sQuery(id+"F0.wireOp",EDGE,"E12"),sQuery(id+"F0.wireOp",EDGE,"E13"),sQuery(id+"F0.wireOp",EDGE,"E14"),sQuery(id+"F0.wireOp",EDGE,"E15"),sQuery(id+"F0.wireOp",EDGE,"E16"),sQuery(id+"F0.wireOp",EDGE,"E17"),sQuery(id+"F0.wireOp",EDGE,"E18"),sQuery(id+"F0.wireOp",EDGE,"E19"),sQuery(id+"F0.wireOp",EDGE,"E20"),sQuery(id+"F0.wireOp",EDGE,"E21"),sQuery(id+"F0.wireOp",EDGE,"E22"),sQuery(id+"F0.wireOp",EDGE,"E23"),sQuery(id+"F0.wireOp",EDGE,"E24"),sQuery(id+"F0.wireOp",EDGE,"E25"),sQuery(id+"F0.wireOp",EDGE,"E26"),sQuery(id+"F0.wireOp",EDGE,"E27"),sQuery(id+"F0.wireOp",EDGE,"E28"),sQuery(id+"F0.wireOp",EDGE,"E29"),sQuery(id+"F0.wireOp",EDGE,"E30"),sQuery(id+"F0.wireOp",EDGE,"E31"),sQuery(id+"F0.wireOp",EDGE,"E32"),sQuery(id+"F0.wireOp",EDGE,"E33"),sQuery(id+"F0.wireOp",EDGE,"E34"),sQuery(id+"F0.wireOp",EDGE,"E35"),sQuery(id+"F0.wireOp",EDGE,"E36"),sQuery(id+"F0.wireOp",EDGE,"E37"),sQuery(id+"F0.wireOp",EDGE,"E38"),sQuery(id+"F0.wireOp",EDGE,"E39"),sQuery(id+"F0.wireOp",EDGE,"E40"),sQuery(id+"F0.wireOp",EDGE,"E41"),sQuery(id+"F0.wireOp",EDGE,"E42"),sQuery(id+"F0.wireOp",EDGE,"E43"),sQuery(id+"F0.wireOp",EDGE,"E44"),sQuery(id+"F0.wireOp",EDGE,"E45"),sQuery(id+"F0.wireOp",EDGE,"E46"),sQuery(id+"F0.wireOp",EDGE,"E47"),sQuery(id+"F0.wireOp",EDGE,"E48"),sQuery(id+"F0.wireOp",EDGE,"E49"),sQuery(id+"F0.wireOp",EDGE,"E50"),sQuery(id+"F0.wireOp",EDGE,"E51"),sQuery(id+"F0.wireOp",EDGE,"E52"),sQuery(id+"F0.wireOp",EDGE,"E53"),sQuery(id+"F0.wireOp",EDGE,"E54"),sQuery(id+"F0.wireOp",EDGE,"E55"),sQuery(id+"F0.wireOp",EDGE,"E56"),sQuery(id+"F0.wireOp",EDGE,"E57"),sQuery(id+"F0.wireOp",EDGE,"E58"),sQuery(id+"F0.wireOp",EDGE,"E59"),sQuery(id+"F0.wireOp",EDGE,"E60"),sQuery(id+"F0.wireOp",EDGE,"E61"),sQuery(id+"F0.wireOp",EDGE,"E62"),sQuery(id+"F0.wireOp",EDGE,"E63"),sQuery(id+"F0.wireOp",EDGE,"E64"),sQuery(id+"F0.wireOp",EDGE,"E65"),sQuery(id+"F0.wireOp",EDGE,"E66"),sQuery(id+"F0.wireOp",EDGE,"E67"),sQuery(id+"F0.wireOp",EDGE,"E68"),sQuery(id+"F0.wireOp",EDGE,"E69"),sQuery(id+"F0.wireOp",EDGE,"E70"),sQuery(id+"F0.wireOp",EDGE,"E71"),sQuery(id+"F0.wireOp",EDGE,"E72"),sQuery(id+"F0.wireOp",EDGE,"E73"),sQuery(id+"F0.wireOp",EDGE,"E74"),sQuery(id+"F0.wireOp",EDGE,"E75"),sQuery(id+"F0.wireOp",EDGE,"E76"),sQuery(id+"F0.wireOp",EDGE,"E77"),sQuery(id+"F0.wireOp",EDGE,"E78"),sQuery(id+"F0.wireOp",EDGE,"E79"),sQuery(id+"F0.wireOp",EDGE,"E80"),sQuery(id+"F0.wireOp",EDGE,"E81"),sQuery(id+"F0.wireOp",EDGE,"E82"),sQuery(id+"F0.wireOp",EDGE,"E83"),sQuery(id+"F0.wireOp",EDGE,"E84"),sQuery(id+"F0.wireOp",EDGE,"E85"),sQuery(id+"F0.wireOp",EDGE,"E86"),sQuery(id+"F0.wireOp",EDGE,"E87"),sQuery(id+"F0.wireOp",EDGE,"E88"),sQuery(id+"F0.wireOp",EDGE,"E89"),sQuery(id+"F0.wireOp",EDGE,"E90"),sQuery(id+"F0.wireOp",EDGE,"E91"),sQuery(id+"F0.wireOp",EDGE,"E92"),sQuery(id+"F0.wireOp",EDGE,"E93"),sQuery(id+"F0.wireOp",EDGE,"E94"),sQuery(id+"F0.wireOp",EDGE,"E95"),sQuery(id+"F0.wireOp",EDGE,"E96"),sQuery(id+"F0.wireOp",EDGE,"E97"),sQuery(id+"F0.wireOp",EDGE,"E98"),sQuery(id+"F0.wireOp",EDGE,"E99"),sQuery(id+"F0.wireOp",EDGE,"E100"),sQuery(id+"F0.wireOp",EDGE,"E101"),sQuery(id+"F0.wireOp",EDGE,"E102"),sQuery(id+"F0.wireOp",EDGE,"E103"),sQuery(id+"F0.wireOp",EDGE,"E104"),sQuery(id+"F0.wireOp",EDGE,"E105"),sQuery(id+"F0.wireOp",EDGE,"E106"),sQuery(id+"F0.wireOp",EDGE,"E107"),sQuery(id+"F0.wireOp",EDGE,"E108"),sQuery(id+"F0.wireOp",EDGE,"E109"),sQuery(id+"F0.wireOp",EDGE,"E110"),sQuery(id+"F0.wireOp",EDGE,"E111"),sQuery(id+"F0.wireOp",EDGE,"E112"),sQuery(id+"F0.wireOp",EDGE,"E113"),sQuery(id+"F0.wireOp",EDGE,"E114"),sQuery(id+"F0.wireOp",EDGE,"E115"),sQuery(id+"F0.wireOp",EDGE,"E116"),sQuery(id+"F0.wireOp",EDGE,"E117"),sQuery(id+"F0.wireOp",EDGE,"E118"),sQuery(id+"F0.wireOp",EDGE,"E119"),sQuery(id+"F0.wireOp",EDGE,"E120"),sQuery(id+"F0.wireOp",EDGE,"E121"),sQuery(id+"F0.wireOp",EDGE,"E122"),sQuery(id+"F0.wireOp",EDGE,"E123"),sQuery(id+"F0.wireOp",EDGE,"E124"),sQuery(id+"F0.wireOp",EDGE,"E125"),sQuery(id+"F0.wireOp",EDGE,"E126"),sQuery(id+"F0.wireOp",EDGE,"E127"),sQuery(id+"F0.wireOp",EDGE,"E128"),sQuery(id+"F0.wireOp",EDGE,"E129"),sQuery(id+"F0.wireOp",EDGE,"E130"),sQuery(id+"F0.wireOp",EDGE,"E131"),sQuery(id+"F0.wireOp",EDGE,"E132"),sQuery(id+"F0.wireOp",EDGE,"E133"),sQuery(id+"F0.wireOp",EDGE,"E134"),sQuery(id+"F0.wireOp",EDGE,"E135"),sQuery(id+"F0.wireOp",EDGE,"E136"),sQuery(id+"F0.wireOp",EDGE,"E137"),sQuery(id+"F0.wireOp",EDGE,"E138"),sQuery(id+"F0.wireOp",EDGE,"E139"),sQuery(id+"F0.wireOp",EDGE,"E140"),sQuery(id+"F0.wireOp",EDGE,"E141"),sQuery(id+"F0.wireOp",EDGE,"E142"),sQuery(id+"F0.wireOp",EDGE,"E143"),sQuery(id+"F0.wireOp",EDGE,"E144"),sQuery(id+"F0.wireOp",EDGE,"E145"),sQuery(id+"F0.wireOp",EDGE,"E146"),sQuery(id+"F0.wireOp",EDGE,"E147"),sQuery(id+"F0.wireOp",EDGE,"E148"),sQuery(id+"F0.wireOp",EDGE,"E149"),sQuery(id+"F0.wireOp",EDGE,"E150"),sQuery(id+"F0.wireOp",EDGE,"E151"),sQuery(id+"F0.wireOp",EDGE,"E152"),sQuery(id+"F0.wireOp",EDGE,"E153"),sQuery(id+"F0.wireOp",EDGE,"E154"),sQuery(id+"F0.wireOp",EDGE,"E155"),sQuery(id+"F0.wireOp",EDGE,"E156"),sQuery(id+"F0.wireOp",EDGE,"E157"),sQuery(id+"F0.wireOp",EDGE,"E158"),sQuery(id+"F0.wireOp",EDGE,"E159"),sQuery(id+"F0.wireOp",EDGE,"E160"),sQuery(id+"F0.wireOp",EDGE,"E161"),sQuery(id+"F0.wireOp",EDGE,"E162"),sQuery(id+"F0.wireOp",EDGE,"E163"),sQuery(id+"F0.wireOp",EDGE,"E164"),sQuery(id+"F0.wireOp",EDGE,"E165"),sQuery(id+"F0.wireOp",EDGE,"E166"),sQuery(id+"F0.wireOp",EDGE,"E167"),sQuery(id+"F0.wireOp",EDGE,"E168"),sQuery(id+"F0.wireOp",EDGE,"E169"),sQuery(id+"F0.wireOp",EDGE,"E170"),sQuery(id+"F0.wireOp",EDGE,"E171"),sQuery(id+"F0.wireOp",EDGE,"E172"),sQuery(id+"F0.wireOp",EDGE,"E173"),sQuery(id+"F0.wireOp",EDGE,"E174"),sQuery(id+"F0.wireOp",EDGE,"E175"),sQuery(id+"F0.wireOp",EDGE,"E176"),sQuery(id+"F0.wireOp",EDGE,"E177"),sQuery(id+"F0.wireOp",EDGE,"E178"),sQuery(id+"F0.wireOp",EDGE,"E179"),sQuery(id+"F0.wireOp",EDGE,"E180"),sQuery(id+"F0.wireOp",EDGE,"E181"),sQuery(id+"F0.wireOp",EDGE,"E182"),sQuery(id+"F0.wireOp",EDGE,"E183"),sQuery(id+"F0.wireOp",EDGE,"E184"),sQuery(id+"F0.wireOp",EDGE,"E185"),sQuery(id+"F0.wireOp",EDGE,"E186"),sQuery(id+"F0.wireOp",EDGE,"E187"),sQuery(id+"F0.wireOp",EDGE,"E188"),sQuery(id+"F0.wireOp",EDGE,"E189"),sQuery(id+"F0.wireOp",EDGE,"E190"),sQuery(id+"F0.wireOp",EDGE,"E191"),sQuery(id+"F0.wireOp",EDGE,"E192"),sQuery(id+"F0.wireOp",EDGE,"E193"),sQuery(id+"F0.wireOp",EDGE,"E194"),sQuery(id+"F0.wireOp",EDGE,"E195"),sQuery(id+"F0.wireOp",EDGE,"E196"),sQuery(id+"F0.wireOp",EDGE,"E197"),sQuery(id+"F0.wireOp",EDGE,"E198"),sQuery(id+"F0.wireOp",EDGE,"E199"),sQuery(id+"F0.wireOp",EDGE,"E200"),sQuery(id+"F0.wireOp",EDGE,"E201"),sQuery(id+"F0.wireOp",EDGE,"E202"),sQuery(id+"F0.wireOp",EDGE,"E203"),sQuery(id+"F0.wireOp",EDGE,"E204"),sQuery(id+"F0.wireOp",EDGE,"E205"),sQuery(id+"F0.wireOp",EDGE,"E206"),sQuery(id+"F0.wireOp",EDGE,"E207"),sQuery(id+"F0.wireOp",EDGE,"E208"),sQuery(id+"F0.wireOp",EDGE,"E209"),sQuery(id+"F0.wireOp",EDGE,"E210"),sQuery(id+"F0.wireOp",EDGE,"E211"),sQuery(id+"F0.wireOp",EDGE,"E212"),sQuery(id+"F0.wireOp",EDGE,"E213"),sQuery(id+"F0.wireOp",EDGE,"E214"),sQuery(id+"F0.wireOp",EDGE,"E215"),sQuery(id+"F0.wireOp",EDGE,"E216"),sQuery(id+"F0.wireOp",EDGE,"E217"),sQuery(id+"F0.wireOp",EDGE,"E218"),sQuery(id+"F0.wireOp",EDGE,"E219"),sQuery(id+"F0.wireOp",EDGE,"E220"),sQuery(id+"F0.wireOp",EDGE,"E221"),sQuery(id+"F0.wireOp",EDGE,"E222"),sQuery(id+"F0.wireOp",EDGE,"E223"),sQuery(id+"F0.wireOp",EDGE,"E224"),sQuery(id+"F0.wireOp",EDGE,"E225"),sQuery(id+"F0.wireOp",EDGE,"E226"),sQuery(id+"F0.wireOp",EDGE,"E227"),sQuery(id+"F0.wireOp",EDGE,"E228"),sQuery(id+"F0.wireOp",EDGE,"E229"),sQuery(id+"F0.wireOp",EDGE,"E230"),sQuery(id+"F0.wireOp",EDGE,"E231"),sQuery(id+"F0.wireOp",EDGE,"E232"),sQuery(id+"F0.wireOp",EDGE,"E233"),sQuery(id+"F0.wireOp",EDGE,"E234"),sQuery(id+"F0.wireOp",EDGE,"E235"),sQuery(id+"F0.wireOp",EDGE,"E236"),sQuery(id+"F0.wireOp",EDGE,"E237"),sQuery(id+"F0.wireOp",EDGE,"E238"),sQuery(id+"F0.wireOp",EDGE,"E239"),sQuery(id+"F0.wireOp",EDGE,"E240"),sQuery(id+"F0.wireOp",EDGE,"E241"),sQuery(id+"F0.wireOp",EDGE,"E242"),sQuery(id+"F0.wireOp",EDGE,"E243"),sQuery(id+"F0.wireOp",EDGE,"E244"),sQuery(id+"F0.wireOp",EDGE,"E245"),sQuery(id+"F0.wireOp",EDGE,"E246"),sQuery(id+"F0.wireOp",EDGE,"E247"),sQuery(id+"F0.wireOp",EDGE,"E248"),sQuery(id+"F0.wireOp",EDGE,"E249"),sQuery(id+"F0.wireOp",EDGE,"E250"),sQuery(id+"F0.wireOp",EDGE,"E251"),sQuery(id+"F0.wireOp",EDGE,"E252"),sQuery(id+"F0.wireOp",EDGE,"E253"),sQuery(id+"F0.wireOp",EDGE,"E254"),sQuery(id+"F0.wireOp",EDGE,"E255"),sQuery(id+"F0.wireOp",EDGE,"E256"),sQuery(id+"F0.wireOp",EDGE,"E257"),sQuery(id+"F0.wireOp",EDGE,"E258"),sQuery(id+"F0.wireOp",EDGE,"E259"),sQuery(id+"F0.wireOp",EDGE,"E260"),sQuery(id+"F0.wireOp",EDGE,"E261"),sQuery(id+"F0.wireOp",EDGE,"E262"),sQuery(id+"F0.wireOp",EDGE,"E263"),sQuery(id+"F0.wireOp",EDGE,"E264"),sQuery(id+"F0.wireOp",EDGE,"E265"),sQuery(id+"F0.wireOp",EDGE,"E266"),sQuery(id+"F0.wireOp",EDGE,"E267"),sQuery(id+"F0.wireOp",EDGE,"E268"),sQuery(id+"F0.wireOp",EDGE,"E269"),sQuery(id+"F0.wireOp",EDGE,"E270"),sQuery(id+"F0.wireOp",EDGE,"E271"),sQuery(id+"F0.wireOp",EDGE,"E272"),sQuery(id+"F0.wireOp",EDGE,"E273"),sQuery(id+"F0.wireOp",EDGE,"E274"),sQuery(id+"F0.wireOp",EDGE,"E275"),sQuery(id+"F0.wireOp",EDGE,"E276"),sQuery(id+"F0.wireOp",EDGE,"E277"),sQuery(id+"F0.wireOp",EDGE,"E278"),sQuery(id+"F0.wireOp",EDGE,"E279"),sQuery(id+"F0.wireOp",EDGE,"E280"),sQuery(id+"F0.wireOp",EDGE,"E281"),sQuery(id+"F0.wireOp",EDGE,"E282"),sQuery(id+"F0.wireOp",EDGE,"E283"),sQuery(id+"F0.wireOp",EDGE,"E284"),sQuery(id+"F0.wireOp",EDGE,"E285"),sQuery(id+"F0.wireOp",EDGE,"E286"),sQuery(id+"F0.wireOp",EDGE,"E287"),sQuery(id+"F0.wireOp",EDGE,"E288"),sQuery(id+"F0.wireOp",EDGE,"E289"),sQuery(id+"F0.wireOp",EDGE,"E290"),sQuery(id+"F0.wireOp",EDGE,"E291"),sQuery(id+"F0.wireOp",EDGE,"E292"),sQuery(id+"F0.wireOp",EDGE,"E293"),sQuery(id+"F0.wireOp",EDGE,"E294"),sQuery(id+"F0.wireOp",EDGE,"E295"),sQuery(id+"F0.wireOp",EDGE,"E296"),sQuery(id+"F0.wireOp",EDGE,"E297"),sQuery(id+"F0.wireOp",EDGE,"E298"),sQuery(id+"F0.wireOp",EDGE,"E299"),sQuery(id+"F0.wireOp",EDGE,"E300"),sQuery(id+"F0.wireOp",EDGE,"E301"),sQuery(id+"F0.wireOp",EDGE,"E302"),sQuery(id+"F0.wireOp",EDGE,"E303"),sQuery(id+"F0.wireOp",EDGE,"E304"),sQuery(id+"F0.wireOp",EDGE,"E305"),sQuery(id+"F0.wireOp",EDGE,"E306"),sQuery(id+"F0.wireOp",EDGE,"E307"),sQuery(id+"F0.wireOp",EDGE,"E308"),sQuery(id+"F0.wireOp",EDGE,"E309"),sQuery(id+"F0.wireOp",EDGE,"E310"),sQuery(id+"F0.wireOp",EDGE,"E311"),sQuery(id+"F0.wireOp",EDGE,"E312"),sQuery(id+"F0.wireOp",EDGE,"E313"),sQuery(id+"F0.wireOp",EDGE,"E314"),sQuery(id+"F0.wireOp",EDGE,"E315"),sQuery(id+"F0.wireOp",EDGE,"E316"),sQuery(id+"F0.wireOp",EDGE,"E317"),sQuery(id+"F0.wireOp",EDGE,"E318"),sQuery(id+"F0.wireOp",EDGE,"E319"),sQuery(id+"F0.wireOp",EDGE,"E320"),sQuery(id+"F0.wireOp",EDGE,"E321"),sQuery(id+"F0.wireOp",EDGE,"E322"),sQuery(id+"F0.wireOp",EDGE,"E323"),sQuery(id+"F0.wireOp",EDGE,"E324"),sQuery(id+"F0.wireOp",EDGE,"E325"),sQuery(id+"F0.wireOp",EDGE,"E326"),sQuery(id+"F0.wireOp",EDGE,"E327"),sQuery(id+"F0.wireOp",EDGE,"E328"),sQuery(id+"F0.wireOp",EDGE,"E329"),sQuery(id+"F0.wireOp",EDGE,"E330"),sQuery(id+"F0.wireOp",EDGE,"E331"),sQuery(id+"F0.wireOp",EDGE,"E332"),sQuery(id+"F0.wireOp",EDGE,"E333"),sQuery(id+"F0.wireOp",EDGE,"E334"),sQuery(id+"F0.wireOp",EDGE,"E335"),sQuery(id+"F0.wireOp",EDGE,"E336"),sQuery(id+"F0.wireOp",EDGE,"E337"),sQuery(id+"F0.wireOp",EDGE,"E338"),sQuery(id+"F0.wireOp",EDGE,"E339"),sQuery(id+"F0.wireOp",EDGE,"E340"),sQuery(id+"F0.wireOp",EDGE,"E341"),sQuery(id+"F0.wireOp",EDGE,"E342"),sQuery(id+"F0.wireOp",EDGE,"E343"),sQuery(id+"F0.wireOp",EDGE,"E344"),sQuery(id+"F0.wireOp",EDGE,"E345"),sQuery(id+"F0.wireOp",EDGE,"E346"),sQuery(id+"F0.wireOp",EDGE,"E347"),sQuery(id+"F0.wireOp",EDGE,"E348"),sQuery(id+"F0.wireOp",EDGE,"E349"),sQuery(id+"F0.wireOp",EDGE,"E350"),sQuery(id+"F0.wireOp",EDGE,"E351"),sQuery(id+"F0.wireOp",EDGE,"E352"),sQuery(id+"F0.wireOp",EDGE,"E353"),sQuery(id+"F0.wireOp",EDGE,"E354"),sQuery(id+"F0.wireOp",EDGE,"E355"),sQuery(id+"F0.wireOp",EDGE,"E356"),sQuery(id+"F0.wireOp",EDGE,"E357"),sQuery(id+"F0.wireOp",EDGE,"E358"),sQuery(id+"F0.wireOp",EDGE,"E359"),sQuery(id+"F0.wireOp",EDGE,"E360"),sQuery(id+"F0.wireOp",EDGE,"E361"),sQuery(id+"F0.wireOp",EDGE,"E362"),sQuery(id+"F0.wireOp",EDGE,"E363"),sQuery(id+"F0.wireOp",EDGE,"E364"),sQuery(id+"F0.wireOp",EDGE,"E365"),sQuery(id+"F0.wireOp",EDGE,"E366"),sQuery(id+"F0.wireOp",EDGE,"E367"),sQuery(id+"F0.wireOp",EDGE,"E368")])],"isStart":true});
            var sketch = newSketch(context, id + "F2", { "sketchPlane" : qUnion([Q0])});
            skCircle(sketch, "E369", {"center": v(9.53, 0) * mm, "radius": 1.59 * mm});
            skCircle(sketch, "E370.1.0", {"center": v(-4.76, 8.25) * mm, "radius": 1.59 * mm});
            skCircle(sketch, "E370.2.0", {"center": v(-4.76, -8.25) * mm, "radius": 1.59 * mm});
            skPoint(sketch, "E370.center", {"position": v(0, 0) * mm});
            skSolve(sketch);
        }
        {
            var Q0;
            Q0=makeQuery(id+"F2.imprint","IMPRINT",FACE,{"disambiguationData":[TD([[makeQuery(id+"F2.imprint","IMPRINT",EDGE,{"derivedFrom":sQuery(id+"F2.wireOp",EDGE,"E370.1.0")}),1.0]])]});
            var Q1;
            Q1 = qSketchRegion(id + "F2", true);
            var Q2;
            Q2=makeQuery(id+"F2.imprint","IMPRINT",FACE,{"disambiguationData":[TD([[makeQuery(id+"F2.imprint","IMPRINT",EDGE,{"derivedFrom":sQuery(id+"F2.wireOp",EDGE,"E370.2.0")}),1.0]])]});
            var Q3;
            Q3=makeQuery(id+"F2.imprint","IMPRINT",FACE,{"disambiguationData":[TD([[makeQuery(id+"F2.imprint","IMPRINT",EDGE,{"derivedFrom":sQuery(id+"F2.wireOp",EDGE,"E369")}),1.0]])]});
            extrude(context, id + "F3", {"entities" : qUnion([Q0, Q1, Q2, Q3]), "operationType" : NewBodyOperationType.REMOVE, "endBound" : BoundingType.THROUGH_ALL, "oppositeDirection" : true, "depth" : 25.4 * mm, "offsetDistance" : 25.4 * mm});
        }
    });
